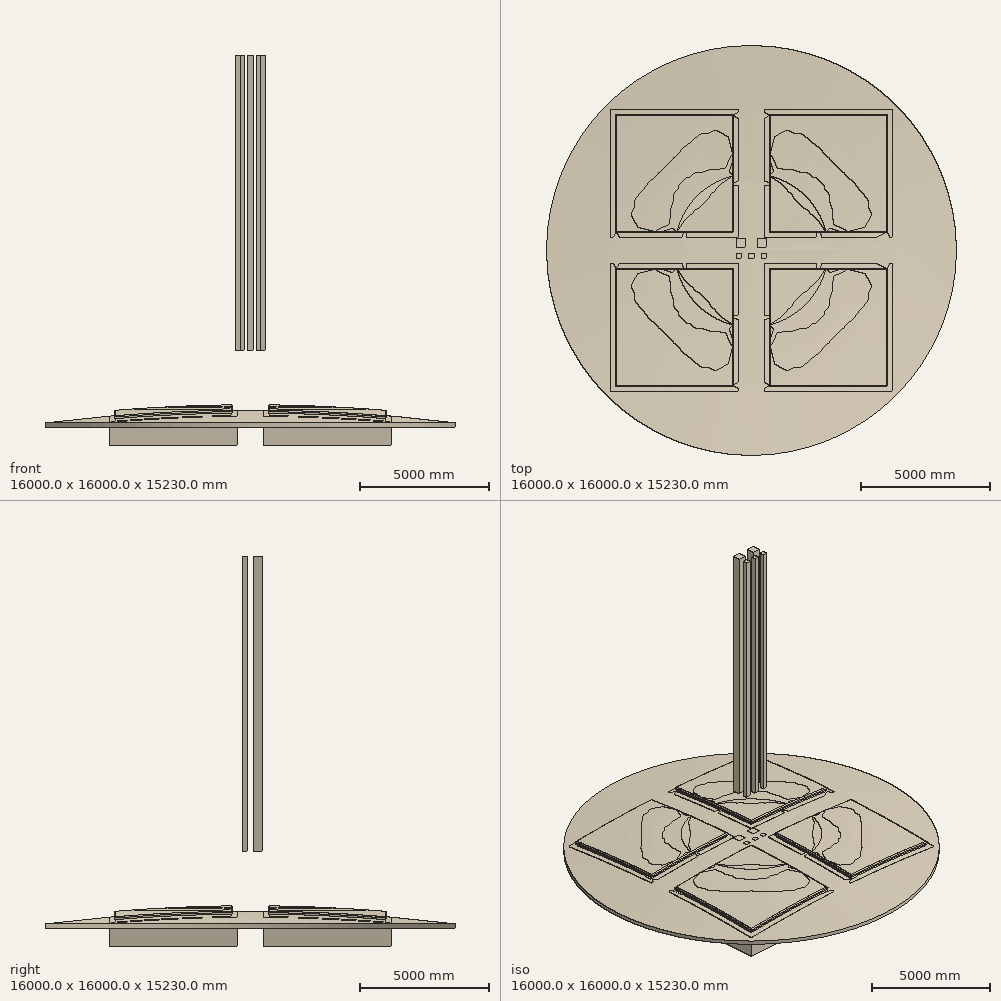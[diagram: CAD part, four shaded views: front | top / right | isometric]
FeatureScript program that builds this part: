
annotation { "Feature Type Name" : "Feature", "Feature Type Description" : "" }
export const myFeature = defineFeature(function(context is Context, id is Id, definition is map)
    precondition{}
    {
        {
            var Q0;
            Q0=qCreatedBy(makeId("Top.planeOp"),FACE);
            cPlane(context, id + "F0", {"entities" : qUnion([Q0]), "cplaneType" : CPlaneType.OFFSET, "offset" : 600 * mm, "width" : 150 * mm, "height" : 150 * mm});
        }
        {
            var Q0;
            Q0=qCreatedBy(makeId("Top.planeOp"),FACE);
            var sketch = newSketch(context, id + "F1", { "sketchPlane" : qUnion([Q0])});
            skCircle(sketch, "E0", {"center": v(0, 0) * mm, "radius": 8000 * mm});
            skLineSegment(sketch, "E1", {"start": v(-8000, 0) * mm, "end": v(8000, 0) * mm, "construction": true});
            skLineSegment(sketch, "E2", {"start": v(0, 8000) * mm, "end": v(0, -8000) * mm, "construction": true});
            skLineSegment(sketch, "E3", {"start": v(300, 7994.37) * mm, "end": v(300, 300) * mm});
            skLineSegment(sketch, "E4", {"start": v(300, 300) * mm, "end": v(7994.37, 300) * mm});
            skLineSegment(sketch, "E5.1.0", {"start": v(-7994.37, 300) * mm, "end": v(-300, 300) * mm});
            skLineSegment(sketch, "E5.1.1", {"start": v(-300, 300) * mm, "end": v(-300, 7994.37) * mm});
            skLineSegment(sketch, "E5.2.0", {"start": v(-300, -7994.37) * mm, "end": v(-300, -300) * mm});
            skLineSegment(sketch, "E5.2.1", {"start": v(-300, -300) * mm, "end": v(-7994.37, -300) * mm});
            skLineSegment(sketch, "E5.3.0", {"start": v(7994.37, -300) * mm, "end": v(300, -300) * mm});
            skLineSegment(sketch, "E5.3.1", {"start": v(300, -300) * mm, "end": v(300, -7994.37) * mm});
            skSolve(sketch);
        }
        {
            var Q0;
            Q0=qCreatedBy(makeId("Front.planeOp"),FACE);
            var sketch = newSketch(context, id + "F2", { "sketchPlane" : qUnion([Q0])});
            skLineSegment(sketch, "E6.0", {"start": v(0, 0) * mm, "end": v(8000, 0) * mm, "construction": true});
            skArc(sketch, "E7", {"start": v(0, 500) * mm, "mid": v(4007.8, 374.88) * mm, "end": v(8000, 0) * mm});
            skLineSegment(sketch, "E8", {"start": v(0, -20) * mm, "end": v(0, 500) * mm});
            skPoint(sketch, "E9.orphan", {"position": v(-8000, 0) * mm});
            skArc(sketch, "E10.0", {"start": v(0, 0) * mm, "mid": v(4007.93, -126.11) * mm, "end": v(8000, -503.95) * mm});
            skLineSegment(sketch, "E11", {"start": v(8000, 0) * mm, "end": v(8000, -524.11) * mm});
            skArc(sketch, "E12.0", {"start": v(0, -20) * mm, "mid": v(4007.93, -146.15) * mm, "end": v(8000, -524.11) * mm});
            skSolve(sketch);
        }
        {
            var Q0;
            Q0=qCreatedBy(id+"F0.planeOp",FACE);
            var sketch = newSketch(context, id + "F3", { "sketchPlane" : qUnion([Q0])});
            skLineSegment(sketch, "E13.bottom", {"start": v(-750, 500) * mm, "end": v(750, 500) * mm});
            skLineSegment(sketch, "E13.top", {"start": v(-750, -500) * mm, "end": v(750, -500) * mm});
            skLineSegment(sketch, "E13.left", {"start": v(-750, 500) * mm, "end": v(-750, -500) * mm});
            skLineSegment(sketch, "E13.right", {"start": v(750, 500) * mm, "end": v(750, -500) * mm});
            skPoint(sketch, "E13.middle", {"position": v(0, 0) * mm});
            skSolve(sketch);
        }
        {
            var Q0;
            Q0=qCreatedBy(makeId("Top.planeOp"),FACE);
            var sketch = newSketch(context, id + "F4", { "sketchPlane" : qUnion([Q0])});
            skLineSegment(sketch, "E14.bottom", {"start": v(-600, 125) * mm, "end": v(-250, 125) * mm});
            skLineSegment(sketch, "E14.top", {"start": v(-600, 475) * mm, "end": v(-250, 475) * mm});
            skLineSegment(sketch, "E14.left", {"start": v(-600, 125) * mm, "end": v(-600, 475) * mm});
            skLineSegment(sketch, "E14.right", {"start": v(-250, 125) * mm, "end": v(-250, 475) * mm});
            skLineSegment(sketch, "E15.0.1.0", {"start": v(-600, -325) * mm, "end": v(-400, -325) * mm});
            skLineSegment(sketch, "E15.0.1.1", {"start": v(-600, -325) * mm, "end": v(-600, -125) * mm});
            skLineSegment(sketch, "E15.0.1.2", {"start": v(-600, -125) * mm, "end": v(-400, -125) * mm});
            skLineSegment(sketch, "E15.0.1.3", {"start": v(-400, -325) * mm, "end": v(-400, -125) * mm});
            skLineSegment(sketch, "E15.1.1.0", {"start": v(-100, -325) * mm, "end": v(100, -325) * mm});
            skLineSegment(sketch, "E15.1.1.1", {"start": v(-100, -325) * mm, "end": v(-100, -125) * mm});
            skLineSegment(sketch, "E15.1.1.2", {"start": v(-100, -125) * mm, "end": v(100, -125) * mm});
            skLineSegment(sketch, "E15.1.1.3", {"start": v(100, -325) * mm, "end": v(100, -125) * mm});
            skLineSegment(sketch, "E15.2.0.0", {"start": v(250, 125) * mm, "end": v(600, 125) * mm});
            skLineSegment(sketch, "E15.2.0.1", {"start": v(250, 125) * mm, "end": v(250, 475) * mm});
            skLineSegment(sketch, "E15.2.0.2", {"start": v(250, 475) * mm, "end": v(600, 475) * mm});
            skLineSegment(sketch, "E15.2.0.3", {"start": v(600, 125) * mm, "end": v(600, 475) * mm});
            skLineSegment(sketch, "E15.2.1.0", {"start": v(400, -325) * mm, "end": v(600, -325) * mm});
            skLineSegment(sketch, "E15.2.1.1", {"start": v(400, -325) * mm, "end": v(400, -125) * mm});
            skLineSegment(sketch, "E15.2.1.2", {"start": v(400, -125) * mm, "end": v(600, -125) * mm});
            skLineSegment(sketch, "E15.2.1.3", {"start": v(600, -325) * mm, "end": v(600, -125) * mm});
            skLineSegment(sketch, "E16", {"start": v(-400, -125) * mm, "end": v(-100, -125) * mm, "construction": true});
            skLineSegment(sketch, "E17", {"start": v(-250, 125) * mm, "end": v(250, 125) * mm, "construction": true});
            skLineSegment(sketch, "E18", {"start": v(0, 0) * mm, "end": v(0, -125) * mm, "construction": true});
            skLineSegment(sketch, "E19", {"start": v(0, 0) * mm, "end": v(0, 125) * mm});
            skSolve(sketch);
        }
        {
            var Q0;
            Q0=makeQuery(id+"F4.imprint","IMPRINT",FACE,{"disambiguationData":[TD([[makeQuery(id+"F4.imprint","IMPRINT",EDGE,{"derivedFrom":sQuery(id+"F4.wireOp",EDGE,"E15.0.1.0")}),1.0]])]});
            var Q1;
            Q1=makeQuery(id+"F4.imprint","IMPRINT",FACE,{"disambiguationData":[TD([[makeQuery(id+"F4.imprint","IMPRINT",EDGE,{"derivedFrom":sQuery(id+"F4.wireOp",EDGE,"E14.bottom")}),1.0]])]});
            var Q2;
            Q2=makeQuery(id+"F4.imprint","IMPRINT",FACE,{"disambiguationData":[TD([[makeQuery(id+"F4.imprint","IMPRINT",EDGE,{"derivedFrom":sQuery(id+"F4.wireOp",EDGE,"E15.1.0.0")}),1.0]])]});
            var Q3;
            Q3=makeQuery(id+"F4.imprint","IMPRINT",FACE,{"disambiguationData":[TD([[makeQuery(id+"F4.imprint","IMPRINT",EDGE,{"derivedFrom":sQuery(id+"F4.wireOp",EDGE,"E15.1.1.0")}),1.0]])]});
            var Q4;
            Q4=makeQuery(id+"F4.imprint","IMPRINT",FACE,{"disambiguationData":[TD([[makeQuery(id+"F4.imprint","IMPRINT",EDGE,{"derivedFrom":sQuery(id+"F4.wireOp",EDGE,"E15.2.1.0")}),1.0]])]});
            var Q5;
            Q5=makeQuery(id+"F4.imprint","IMPRINT",FACE,{"disambiguationData":[TD([[makeQuery(id+"F4.imprint","IMPRINT",EDGE,{"derivedFrom":sQuery(id+"F4.wireOp",EDGE,"E15.2.0.0")}),1.0]])]});
            extrude(context, id + "F5", {"entities" : qUnion([Q0, Q1, Q2, Q3, Q4, Q5]), "depth" : 14000 * mm});
        }
        {
            var Q0;
            Q0=qCreatedBy(makeId("Top.planeOp"),FACE);
            var sketch = newSketch(context, id + "F6", { "sketchPlane" : qUnion([Q0])});
            skCircle(sketch, "E20.0", {"center": v(0, 0) * mm, "radius": 8000 * mm});
            skLineSegment(sketch, "E21.0", {"start": v(-8000, 0) * mm, "end": v(8000, 0) * mm, "construction": true});
            skLineSegment(sketch, "E22.0", {"start": v(0, 8000) * mm, "end": v(0, -8000) * mm, "construction": true});
            skLineSegment(sketch, "E23.bottom", {"start": v(-500, 5500) * mm, "end": v(-5500, 5500) * mm});
            skLineSegment(sketch, "E23.top", {"start": v(-500, 500) * mm, "end": v(-5500, 500) * mm});
            skLineSegment(sketch, "E23.left", {"start": v(-500, 5500) * mm, "end": v(-500, 500) * mm});
            skLineSegment(sketch, "E23.right", {"start": v(-5500, 5500) * mm, "end": v(-5500, 500) * mm});
            skLineSegment(sketch, "E24.0", {"start": v(-750, 5250) * mm, "end": v(-750, 750) * mm});
            skLineSegment(sketch, "E24.1", {"start": v(-750, 5250) * mm, "end": v(-5250, 5250) * mm});
            skLineSegment(sketch, "E24.2", {"start": v(-5250, 5250) * mm, "end": v(-5250, 750) * mm});
            skLineSegment(sketch, "E24.3", {"start": v(-750, 750) * mm, "end": v(-5250, 750) * mm});
            skLineSegment(sketch, "E25", {"start": v(-500, 500) * mm, "end": v(-500, 0) * mm, "construction": true});
            skLineSegment(sketch, "E26", {"start": v(-500, 500) * mm, "end": v(0, 500) * mm, "construction": true});
            skSolve(sketch);
        }
        {
            var Q0;
            Q0=makeQuery(id+"F6.imprint","IMPRINT",FACE,{"disambiguationData":[TD([[makeQuery(id+"F6.imprint","IMPRINT",EDGE,{"derivedFrom":sQuery(id+"F6.wireOp",EDGE,"E23.bottom")}),1.0]])]});
            extrude(context, id + "F7", {"entities" : qUnion([Q0]), "operationType" : NewBodyOperationType.ADD, "depth" : 2460 * mm, "symmetric" : true});
        }
        {
            var Q0;
            {var subQ2=sQuery(id+"F2.wireOp",EDGE,"E10.0");Q0=makeQuery(id+"F2.imprint","IMPRINT",FACE,{"disambiguationData":[TD([[makeQuery(id+"F2.imprint","IMPRINT",EDGE,{"derivedFrom":subQ2}),-1.0]])]});}
            var Q1;
            Q1=sQuery(id+"F2.wireOp",EDGE,"E8");
            revolve(context, id + "F8", {"entities" : qUnion([Q0]), "axis" : qUnion([Q1]), "revolveType" : RevolveType.FULL});
        }
        {
            var Q0;
            Q0=qCreatedBy(makeId("Front.planeOp"),FACE);
            var sketch = newSketch(context, id + "F9", { "sketchPlane" : qUnion([Q0])});
            skArc(sketch, "E27.0", {"start": v(0, 500) * mm, "mid": v(4007.8, 374.88) * mm, "end": v(8000, 0) * mm, "construction": true});
            skLineSegment(sketch, "E28", {"start": v(0, 160) * mm, "end": v(0, 2475.89) * mm});
            skLineSegment(sketch, "E29", {"start": v(0, 2475.89) * mm, "end": v(8000, 2475.89) * mm});
            skLineSegment(sketch, "E30", {"start": v(8000, 2475.89) * mm, "end": v(8000, -342.68) * mm});
            skArc(sketch, "E31.0", {"start": v(0, 0) * mm, "mid": v(4007.93, -126.11) * mm, "end": v(8000, -503.95) * mm});
            skLineSegment(sketch, "E32", {"start": v(0, 0) * mm, "end": v(0, -2000) * mm});
            skLineSegment(sketch, "E33", {"start": v(0, -2000) * mm, "end": v(8000, -2000) * mm});
            skLineSegment(sketch, "E34", {"start": v(8000, -2000) * mm, "end": v(8000, -503.95) * mm});
            skArc(sketch, "E35.0", {"start": v(0, 160) * mm, "mid": v(4007.89, 34.2) * mm, "end": v(8000, -342.68) * mm});
            skArc(sketch, "E36.0", {"start": v(0, 260) * mm, "mid": v(4007.86, 134.4) * mm, "end": v(8000, -241.89) * mm});
            skArc(sketch, "E37.0", {"start": v(0, 370) * mm, "mid": v(4007.84, 244.62) * mm, "end": v(8000, -131.02) * mm});
            skSolve(sketch);
        }
        {
            var Q0;
            Q0=makeQuery(id+"F9.imprint","IMPRINT",FACE,{"disambiguationData":[TD([[makeQuery(id+"F9.imprint","IMPRINT",EDGE,{"derivedFrom":sQuery(id+"F9.wireOp",EDGE,"E28")}),-1.0]])]});
            var Q1;
            Q1=makeQuery(id+"F9.imprint","IMPRINT",FACE,{"disambiguationData":[TD([[makeQuery(id+"F9.imprint","IMPRINT",EDGE,{"derivedFrom":sQuery(id+"F9.wireOp",EDGE,"E31.0")}),-1.0]])]});
            var Q2;
            Q2=sQuery(id+"F9.wireOp",EDGE,"E32");
            revolve(context, id + "F10", {"operationType" : NewBodyOperationType.REMOVE, "entities" : qUnion([Q0, Q1]), "axis" : qUnion([Q2]), "revolveType" : RevolveType.FULL, "oppositeDirection" : true});
        }
        {
            var Q0;
            Q0=qCreatedBy(makeId("Top.planeOp"),FACE);
            cPlane(context, id + "F11", {"entities" : qUnion([Q0]), "cplaneType" : CPlaneType.OFFSET, "offset" : 300 * mm, "width" : 150 * mm, "height" : 150 * mm});
        }
        {
            var Q0;
            Q0=qCreatedBy(id+"F11.planeOp",FACE);
            var sketch = newSketch(context, id + "F12", { "sketchPlane" : qUnion([Q0])});
            skLineSegment(sketch, "E38.0", {"start": v(-750, 750) * mm, "end": v(-750, 5250) * mm});
            skLineSegment(sketch, "E39.0", {"start": v(-5250, 5250) * mm, "end": v(-750, 5250) * mm});
            skLineSegment(sketch, "E40.0", {"start": v(-5250, 750) * mm, "end": v(-750, 750) * mm});
            skLineSegment(sketch, "E41.0", {"start": v(-5250, 750) * mm, "end": v(-5250, 5250) * mm});
            skSolve(sketch);
        }
        {
            var Q0;
            Q0=makeQuery(id+"F12.imprint","IMPRINT",FACE,{"disambiguationData":[TD([[makeQuery(id+"F12.imprint","IMPRINT",EDGE,{"derivedFrom":sQuery(id+"F12.wireOp",EDGE,"E38.0")}),1.0]])]});
            var Q1;
            Q1=makeQuery(id+"F8.opRevolve","SWEPT_BODY",BODY,{"disambiguationData":[OSD([sQuery(id+"F2.wireOp",EDGE,"E8"),sQuery(id+"F2.wireOp",EDGE,"E10.0"),sQuery(id+"F2.wireOp",EDGE,"E11"),sQuery(id+"F2.wireOp",EDGE,"E12.0")])]});
            extrude(context, id + "F13", {"entities" : qUnion([Q0]), "endBound" : BoundingType.UP_TO_BODY, "oppositeDirection" : true, "endBoundEntityBody" : qUnion([Q1]), "depth" : 25 * mm});
        }
        {
            var Q0;
            {var subQ0=sQuery(id+"F9.wireOp",EDGE,"E29");Q0=makeQuery(id+"F9.imprint","IMPRINT",FACE,{"disambiguationData":[TD([[makeQuery(id+"F9.imprint","IMPRINT",EDGE,{"derivedFrom":subQ0}),-1.0]])]});}
            var Q1;
            {var subQ0=sQuery(id+"F9.wireOp",EDGE,"E36.0");Q1=makeQuery(id+"F9.imprint","IMPRINT",FACE,{"disambiguationData":[TD([[makeQuery(id+"F9.imprint","IMPRINT",EDGE,{"derivedFrom":subQ0}),1.0]])]});}
            var Q2;
            Q2=sQuery(id+"F9.wireOp",EDGE,"E32");
            revolve(context, id + "F14", {"operationType" : NewBodyOperationType.REMOVE, "entities" : qUnion([Q0, Q1]), "axis" : qUnion([Q2]), "revolveType" : RevolveType.FULL, "oppositeDirection" : true});
        }
        {
            var Q0;
            Q0=makeQuery(id+"F7.opExtrude","SWEPT_BODY",BODY,{"disambiguationData":[OSD([sQuery(id+"F6.wireOp",EDGE,"E23.bottom"),sQuery(id+"F6.wireOp",EDGE,"E23.top"),sQuery(id+"F6.wireOp",EDGE,"E23.left"),sQuery(id+"F6.wireOp",EDGE,"E23.right"),sQuery(id+"F6.wireOp",EDGE,"E24.0"),sQuery(id+"F6.wireOp",EDGE,"E24.1"),sQuery(id+"F6.wireOp",EDGE,"E24.2"),sQuery(id+"F6.wireOp",EDGE,"E24.3")])]});
            var Q1;
            Q1=makeQuery(id+"F13.opExtrude","SWEPT_BODY",BODY,{"disambiguationData":[OSD([sQuery(id+"F12.wireOp",EDGE,"E38.0"),sQuery(id+"F12.wireOp",EDGE,"E39.0"),sQuery(id+"F12.wireOp",EDGE,"E40.0"),sQuery(id+"F12.wireOp",EDGE,"E41.0")])]});
            var Q2;
            Q2=makeQuery(id+"F18.opExtrude","SWEPT_BODY",BODY,{"disambiguationData":[OSD([sQuery(id+"F17.wireOp",EDGE,"E43.0"),sQuery(id+"F17.wireOp",EDGE,"E43.1"),sQuery(id+"F17.wireOp",EDGE,"E43.2"),sQuery(id+"F17.wireOp",EDGE,"E43.3")])]});
            var Q3;
            Q3=sQuery(id+"F9.wireOp",EDGE,"E32");
            circularPattern(context, id + "F15", {"entities" : qUnion([Q0, Q1, Q2]), "axis" : qUnion([Q3]), "angle" : 360 * degree, "instanceCount" : 4, "equalSpace" : true, "computeTransformsWithoutBuiltin" : true});
        }
        {
            var Q0;
            Q0=qCreatedBy(id+"F11.planeOp",FACE);
            cPlane(context, id + "F16", {"entities" : qUnion([Q0]), "cplaneType" : CPlaneType.OFFSET, "offset" : 290 * mm, "width" : 150 * mm, "height" : 150 * mm});
        }
        {
            var Q0;
            Q0=qCreatedBy(id+"F16.planeOp",FACE);
            var sketch = newSketch(context, id + "F17", { "sketchPlane" : qUnion([Q0])});
            skLineSegment(sketch, "E42.0.0", {"start": v(-5250, 750) * mm, "end": v(-750, 750) * mm, "construction": true});
            skLineSegment(sketch, "E42.0.1", {"start": v(-750, 750) * mm, "end": v(-750, 5250) * mm, "construction": true});
            skLineSegment(sketch, "E42.0.2", {"start": v(-5250, 5250) * mm, "end": v(-750, 5250) * mm, "construction": true});
            skLineSegment(sketch, "E42.0.3", {"start": v(-5250, 750) * mm, "end": v(-5250, 5250) * mm, "construction": true});
            skLineSegment(sketch, "E43.0", {"start": v(-5300, 700) * mm, "end": v(-700, 700) * mm});
            skLineSegment(sketch, "E43.1", {"start": v(-5300, 700) * mm, "end": v(-5300, 5300) * mm});
            skLineSegment(sketch, "E43.2", {"start": v(-5300, 5300) * mm, "end": v(-700, 5300) * mm});
            skLineSegment(sketch, "E43.3", {"start": v(-700, 700) * mm, "end": v(-700, 5300) * mm});
            skLineSegment(sketch, "E44.0", {"start": v(-745, 745) * mm, "end": v(-745, 5255) * mm, "construction": true});
            skLineSegment(sketch, "E44.1", {"start": v(-5255, 745) * mm, "end": v(-745, 745) * mm, "construction": true});
            skLineSegment(sketch, "E44.2", {"start": v(-5255, 745) * mm, "end": v(-5255, 5255) * mm, "construction": true});
            skLineSegment(sketch, "E44.3", {"start": v(-5255, 5255) * mm, "end": v(-745, 5255) * mm, "construction": true});
            skLineSegment(sketch, "E45.1.0", {"start": v(-750, -750) * mm, "end": v(-5250, -750) * mm, "construction": true});
            skLineSegment(sketch, "E45.1.1", {"start": v(-5250, -5250) * mm, "end": v(-5250, -750) * mm, "construction": true});
            skLineSegment(sketch, "E45.1.2", {"start": v(-745, -5255) * mm, "end": v(-745, -745) * mm, "construction": true});
            skLineSegment(sketch, "E45.1.3", {"start": v(-700, -5300) * mm, "end": v(-700, -700) * mm});
            skLineSegment(sketch, "E45.1.4", {"start": v(-5255, -5255) * mm, "end": v(-5255, -745) * mm, "construction": true});
            skLineSegment(sketch, "E45.1.5", {"start": v(-750, -5250) * mm, "end": v(-5250, -5250) * mm, "construction": true});
            skLineSegment(sketch, "E45.1.6", {"start": v(-700, -700) * mm, "end": v(-5300, -700) * mm});
            skLineSegment(sketch, "E45.1.7", {"start": v(-5300, -5300) * mm, "end": v(-5300, -700) * mm});
            skLineSegment(sketch, "E45.1.8", {"start": v(-750, -5250) * mm, "end": v(-750, -750) * mm, "construction": true});
            skLineSegment(sketch, "E45.1.9", {"start": v(-700, -5300) * mm, "end": v(-5300, -5300) * mm});
            skLineSegment(sketch, "E45.1.10", {"start": v(-745, -745) * mm, "end": v(-5255, -745) * mm, "construction": true});
            skLineSegment(sketch, "E45.1.11", {"start": v(-745, -5255) * mm, "end": v(-5255, -5255) * mm, "construction": true});
            skLineSegment(sketch, "E45.2.0", {"start": v(750, -750) * mm, "end": v(750, -5250) * mm, "construction": true});
            skLineSegment(sketch, "E45.2.1", {"start": v(5250, -5250) * mm, "end": v(750, -5250) * mm, "construction": true});
            skLineSegment(sketch, "E45.2.2", {"start": v(5255, -745) * mm, "end": v(745, -745) * mm, "construction": true});
            skLineSegment(sketch, "E45.2.3", {"start": v(5300, -700) * mm, "end": v(700, -700) * mm});
            skLineSegment(sketch, "E45.2.4", {"start": v(5255, -5255) * mm, "end": v(745, -5255) * mm, "construction": true});
            skLineSegment(sketch, "E45.2.5", {"start": v(5250, -750) * mm, "end": v(5250, -5250) * mm, "construction": true});
            skLineSegment(sketch, "E45.2.6", {"start": v(700, -700) * mm, "end": v(700, -5300) * mm});
            skLineSegment(sketch, "E45.2.7", {"start": v(5300, -5300) * mm, "end": v(700, -5300) * mm});
            skLineSegment(sketch, "E45.2.8", {"start": v(5250, -750) * mm, "end": v(750, -750) * mm, "construction": true});
            skLineSegment(sketch, "E45.2.9", {"start": v(5300, -700) * mm, "end": v(5300, -5300) * mm});
            skLineSegment(sketch, "E45.2.10", {"start": v(745, -745) * mm, "end": v(745, -5255) * mm, "construction": true});
            skLineSegment(sketch, "E45.2.11", {"start": v(5255, -745) * mm, "end": v(5255, -5255) * mm, "construction": true});
            skLineSegment(sketch, "E45.3.0", {"start": v(750, 750) * mm, "end": v(5250, 750) * mm, "construction": true});
            skLineSegment(sketch, "E45.3.1", {"start": v(5250, 5250) * mm, "end": v(5250, 750) * mm, "construction": true});
            skLineSegment(sketch, "E45.3.2", {"start": v(745, 5255) * mm, "end": v(745, 745) * mm, "construction": true});
            skLineSegment(sketch, "E45.3.3", {"start": v(700, 5300) * mm, "end": v(700, 700) * mm});
            skLineSegment(sketch, "E45.3.4", {"start": v(5255, 5255) * mm, "end": v(5255, 745) * mm, "construction": true});
            skLineSegment(sketch, "E45.3.5", {"start": v(750, 5250) * mm, "end": v(5250, 5250) * mm, "construction": true});
            skLineSegment(sketch, "E45.3.6", {"start": v(700, 700) * mm, "end": v(5300, 700) * mm});
            skLineSegment(sketch, "E45.3.7", {"start": v(5300, 5300) * mm, "end": v(5300, 700) * mm});
            skLineSegment(sketch, "E45.3.8", {"start": v(750, 5250) * mm, "end": v(750, 750) * mm, "construction": true});
            skLineSegment(sketch, "E45.3.9", {"start": v(700, 5300) * mm, "end": v(5300, 5300) * mm});
            skLineSegment(sketch, "E45.3.10", {"start": v(745, 745) * mm, "end": v(5255, 745) * mm, "construction": true});
            skLineSegment(sketch, "E45.3.11", {"start": v(745, 5255) * mm, "end": v(5255, 5255) * mm, "construction": true});
            skPoint(sketch, "E45.center", {"position": v(0, 0) * mm});
            skSolve(sketch);
        }
        {
            var Q0;
            Q0=makeQuery(id+"F17.imprint","IMPRINT",FACE,{"disambiguationData":[TD([[makeQuery(id+"F17.imprint","IMPRINT",EDGE,{"derivedFrom":sQuery(id+"F17.wireOp",EDGE,"E43.0")}),1.0]])]});
            var Q1;
            Q1=makeQuery(id+"F14.boolean.opBoolean","COPY",FACE,{"derivedFrom":makeQuery(id+"F14.opRevolve","SWEPT_FACE",FACE,{"disambiguationData":[OSD([sQuery(id+"F9.wireOp",EDGE,"E36.0")])]})});
            var Q2;
            Q2=makeQuery(id+"F13.opExtrude","SWEPT_BODY",BODY,{"disambiguationData":[OSD([sQuery(id+"F12.wireOp",EDGE,"E38.0"),sQuery(id+"F12.wireOp",EDGE,"E39.0"),sQuery(id+"F12.wireOp",EDGE,"E40.0"),sQuery(id+"F12.wireOp",EDGE,"E41.0")])]});
            extrude(context, id + "F18", {"entities" : qUnion([Q0]), "endBound" : BoundingType.UP_TO_SURFACE, "oppositeDirection" : true, "endBoundEntityFace" : qUnion([Q1]), "endBoundEntityBody" : qUnion([Q2]), "depth" : 25 * mm});
        }
        {
            var Q0;
            Q0=makeQuery(id+"F17.imprint","IMPRINT",FACE,{"disambiguationData":[TD([[makeQuery(id+"F17.imprint","IMPRINT",EDGE,{"derivedFrom":sQuery(id+"F17.wireOp",EDGE,"E45.3.3")}),1.0]])]});
            var Q1;
            Q1=makeQuery(id+"F15.opPattern","COPY",FACE,{"derivedFrom":makeQuery(id+"F14.boolean.opBoolean","COPY",FACE,{"derivedFrom":makeQuery(id+"F14.opRevolve","SWEPT_FACE",FACE,{"disambiguationData":[OSD([sQuery(id+"F9.wireOp",EDGE,"E36.0")])]})}),"instanceName":"1"});
            extrude(context, id + "F19", {"entities" : qUnion([Q0]), "endBound" : BoundingType.UP_TO_SURFACE, "oppositeDirection" : true, "endBoundEntityFace" : qUnion([Q1]), "depth" : 25 * mm});
        }
        {
            var Q0;
            Q0=makeQuery(id+"F17.imprint","IMPRINT",FACE,{"disambiguationData":[TD([[makeQuery(id+"F17.imprint","IMPRINT",EDGE,{"derivedFrom":sQuery(id+"F17.wireOp",EDGE,"E45.2.3")}),1.0]])]});
            var Q1;
            Q1=makeQuery(id+"F15.opPattern","COPY",FACE,{"derivedFrom":makeQuery(id+"F14.boolean.opBoolean","COPY",FACE,{"derivedFrom":makeQuery(id+"F14.opRevolve","SWEPT_FACE",FACE,{"disambiguationData":[OSD([sQuery(id+"F9.wireOp",EDGE,"E36.0")])]})}),"instanceName":"2"});
            extrude(context, id + "F20", {"entities" : qUnion([Q0]), "endBound" : BoundingType.UP_TO_SURFACE, "oppositeDirection" : true, "endBoundEntityFace" : qUnion([Q1]), "depth" : 25 * mm});
        }
        {
            var Q0;
            Q0=makeQuery(id+"F17.imprint","IMPRINT",FACE,{"disambiguationData":[TD([[makeQuery(id+"F17.imprint","IMPRINT",EDGE,{"derivedFrom":sQuery(id+"F17.wireOp",EDGE,"E45.1.3")}),1.0]])]});
            var Q1;
            Q1=makeQuery(id+"F15.opPattern","COPY",FACE,{"derivedFrom":makeQuery(id+"F14.boolean.opBoolean","COPY",FACE,{"derivedFrom":makeQuery(id+"F14.opRevolve","SWEPT_FACE",FACE,{"disambiguationData":[OSD([sQuery(id+"F9.wireOp",EDGE,"E36.0")])]})}),"instanceName":"3"});
            extrude(context, id + "F21", {"entities" : qUnion([Q0]), "endBound" : BoundingType.UP_TO_SURFACE, "oppositeDirection" : true, "endBoundEntityFace" : qUnion([Q1]), "depth" : 25 * mm});
        }
        {
            var Q0;
            {var subQ0=sQuery(id+"F9.wireOp",EDGE,"E29");Q0=makeQuery(id+"F9.imprint","IMPRINT",FACE,{"disambiguationData":[TD([[makeQuery(id+"F9.imprint","IMPRINT",EDGE,{"derivedFrom":subQ0}),-1.0]])]});}
            var Q1;
            Q1=sQuery(id+"F9.wireOp",EDGE,"E32");
            revolve(context, id + "F22", {"operationType" : NewBodyOperationType.REMOVE, "entities" : qUnion([Q0]), "axis" : qUnion([Q1]), "revolveType" : RevolveType.FULL, "oppositeDirection" : true});
        }
        {
            var Q0;
            Q0=makeQuery(id+"F22.boolean.opBoolean","COPY",FACE,{"disambiguationData":[TD([makeQuery(id+"F18.opExtrude","SWEPT_FACE",FACE,{"disambiguationData":[OSD([sQuery(id+"F17.wireOp",EDGE,"E43.0")])]})])],"derivedFrom":makeQuery(id+"F22.opRevolve","SWEPT_FACE",FACE,{"disambiguationData":[OSD([sQuery(id+"F9.wireOp",EDGE,"E37.0")])]})});
            var Q1;
            Q1=makeQuery(id+"F18.opExtrude","CAP_FACE",FACE,{"disambiguationData":[OSD([sQuery(id+"F9.wireOp",EDGE,"E36.0")])],"isStart":false});
            var Q2;
            Q2=makeQuery(id+"F19.opExtrude","CAP_FACE",FACE,{"disambiguationData":[OSD([sQuery(id+"F9.wireOp",EDGE,"E36.0")])],"isStart":false});
            var Q3;
            Q3=makeQuery(id+"F22.boolean.opBoolean","COPY",FACE,{"disambiguationData":[TD([makeQuery(id+"F19.opExtrude","SWEPT_FACE",FACE,{"disambiguationData":[OSD([sQuery(id+"F17.wireOp",EDGE,"E45.3.3")])]})])],"derivedFrom":makeQuery(id+"F22.opRevolve","SWEPT_FACE",FACE,{"disambiguationData":[OSD([sQuery(id+"F9.wireOp",EDGE,"E37.0")])]})});
            var Q4;
            Q4=makeQuery(id+"F22.boolean.opBoolean","COPY",FACE,{"disambiguationData":[TD([makeQuery(id+"F20.opExtrude","SWEPT_FACE",FACE,{"disambiguationData":[OSD([sQuery(id+"F17.wireOp",EDGE,"E45.2.3")])]})])],"derivedFrom":makeQuery(id+"F22.opRevolve","SWEPT_FACE",FACE,{"disambiguationData":[OSD([sQuery(id+"F9.wireOp",EDGE,"E37.0")])]})});
            var Q5;
            Q5=makeQuery(id+"F20.opExtrude","CAP_FACE",FACE,{"disambiguationData":[OSD([sQuery(id+"F9.wireOp",EDGE,"E36.0")])],"isStart":false});
            var Q6;
            Q6=makeQuery(id+"F22.boolean.opBoolean","COPY",FACE,{"disambiguationData":[TD([makeQuery(id+"F21.opExtrude","SWEPT_FACE",FACE,{"disambiguationData":[OSD([sQuery(id+"F17.wireOp",EDGE,"E45.1.3")])]})])],"derivedFrom":makeQuery(id+"F22.opRevolve","SWEPT_FACE",FACE,{"disambiguationData":[OSD([sQuery(id+"F9.wireOp",EDGE,"E37.0")])]})});
            var Q7;
            Q7=makeQuery(id+"F21.opExtrude","CAP_FACE",FACE,{"disambiguationData":[OSD([sQuery(id+"F9.wireOp",EDGE,"E36.0")])],"isStart":false});
            fillet(context, id + "F23", {"entities" : qUnion([Q0, Q1, Q2, Q3, Q4, Q5, Q6, Q7]), "radius" : 50 * mm, "tangentPropagation" : true, "allowEdgeOverflow" : false});
        }
    });
